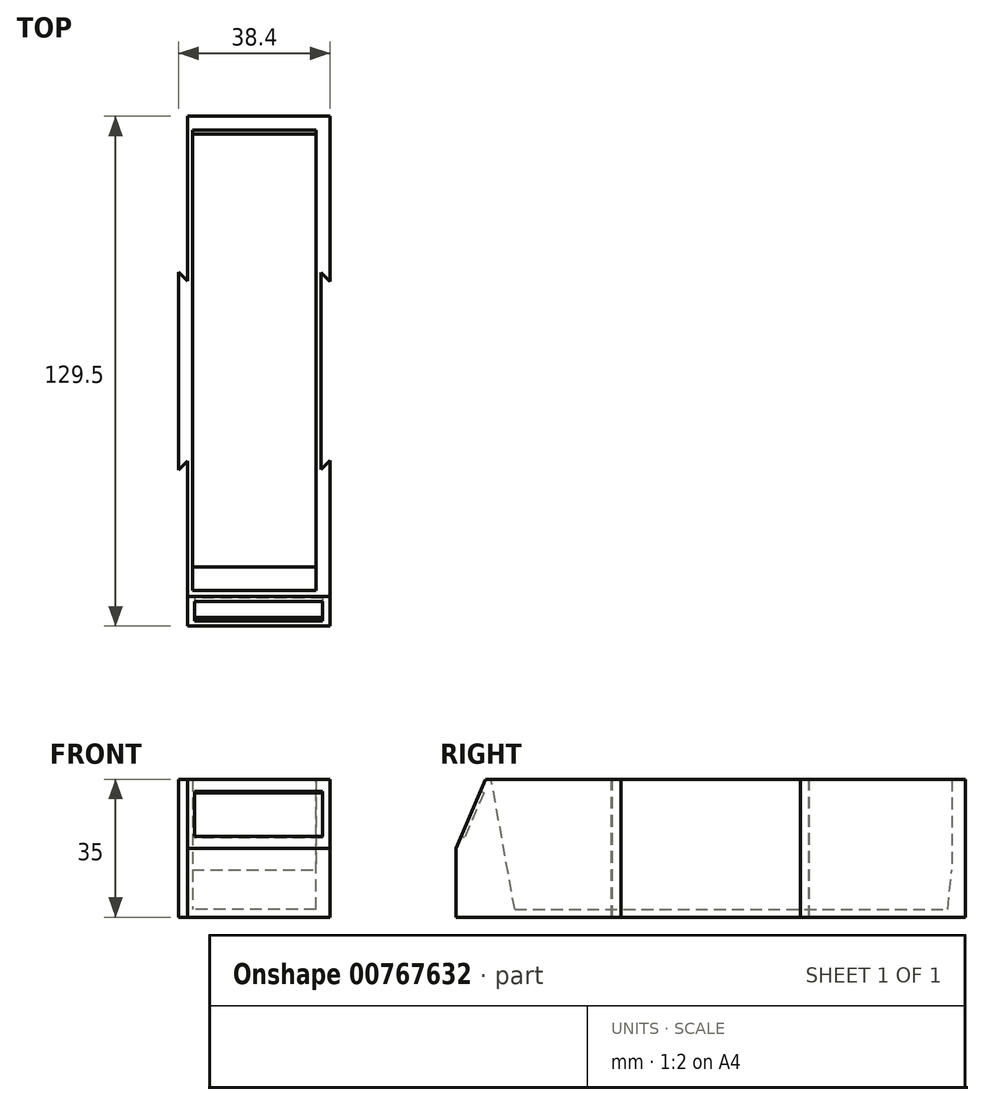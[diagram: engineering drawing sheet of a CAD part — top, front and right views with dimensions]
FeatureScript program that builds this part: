
annotation { "Feature Type Name" : "Feature", "Feature Type Description" : "" }
export const myFeature = defineFeature(function(context is Context, id is Id, definition is map)
    precondition{}
    {
        {
            var Q0;
            Q0=qCreatedBy(makeId("Top.planeOp"),FACE);
            var sketch = newSketch(context, id + "F0", { "sketchPlane" : qUnion([Q0])});
            skLineSegment(sketch, "E0.bottom", {"start": v(15.7, 55.5) * mm, "end": v(-15.7, 55.5) * mm});
            skLineSegment(sketch, "E0.top", {"start": v(15.7, -55.5) * mm, "end": v(-15.7, -55.5) * mm});
            skLineSegment(sketch, "E0.left", {"start": v(15.7, 55.5) * mm, "end": v(15.7, -55.5) * mm});
            skLineSegment(sketch, "E0.right", {"start": v(-15.7, 55.5) * mm, "end": v(-15.7, -55.5) * mm});
            skPoint(sketch, "E0.middle", {"position": v(0, 0) * mm});
            skLineSegment(sketch, "E1.bottom", {"start": v(19.2, -70.5) * mm, "end": v(-19.2, -70.5) * mm});
            skLineSegment(sketch, "E1.top", {"start": v(19.2, 59) * mm, "end": v(-19.2, 59) * mm});
            skLineSegment(sketch, "E1.left", {"start": v(19.2, -70.5) * mm, "end": v(19.2, 59) * mm});
            skLineSegment(sketch, "E1.right", {"start": v(-19.2, -70.5) * mm, "end": v(-19.2, 59) * mm});
            skPoint(sketch, "E1.middle", {"position": v(0, -5.75) * mm});
            skSolve(sketch);
        }
        {
            var Q0;
            Q0=qSketchRegion(id+"F0",true);
            var Q1;
            Q1=makeQuery(id+"F0.imprint","IMPRINT",FACE,{"disambiguationData":[TD([[makeQuery(id+"F0.imprint","IMPRINT",EDGE,{"derivedFrom":sQuery(id+"F0.wireOp",EDGE,"E0.bottom")}),1.0]])]});
            extrude(context, id + "F1", {"entities" : qUnion([Q0, Q1]), "depth" : 2 * mm, "offsetDistance" : 25 * mm});
        }
        {
            var Q0;
            Q0=makeQuery(id+"F0.imprint","IMPRINT",FACE,{"disambiguationData":[TD([[makeQuery(id+"F0.imprint","IMPRINT",EDGE,{"derivedFrom":sQuery(id+"F0.wireOp",EDGE,"E0.bottom")}),-1.0]])]});
            extrude(context, id + "F2", {"entities" : qUnion([Q0]), "operationType" : NewBodyOperationType.ADD, "depth" : 35 * mm, "offsetDistance" : 25 * mm});
        }
        {
            var Q0;
            Q0=makeQuery(id+"F2.opExtrude","CAP_EDGE",EDGE,{"disambiguationData":[OSD([sQuery(id+"F0.wireOp",EDGE,"E1.bottom")])],"isStart":false});
            chamfer(context, id + "F3", {"entities" : qUnion([Q0]), "chamferType" : ChamferType.TWO_OFFSETS, "width1" : 7.5 * mm, "oppositeDirection" : true, "width2" : 17.5 * mm, "tangentPropagation" : true});
        }
        {
            var Q0;
            Q0=makeQuery(id+"F2.opExtrude","CAP_EDGE",EDGE,{"disambiguationData":[OSD([sQuery(id+"F0.wireOp",EDGE,"E0.top")])],"isStart":false});
            chamfer(context, id + "F4", {"entities" : qUnion([Q0]), "chamferType" : ChamferType.TWO_OFFSETS, "width1" : 6 * mm, "oppositeDirection" : false, "width2" : 33 * mm, "tangentPropagation" : true});
        }
        {
            var Q0;
            Q0=makeQuery(id+"F2.opExtrude","CAP_FACE",FACE,{"disambiguationData":[OSD([sQuery(id+"F0.wireOp",EDGE,"E0.bottom"),sQuery(id+"F0.wireOp",EDGE,"E0.top"),sQuery(id+"F0.wireOp",EDGE,"E0.left"),sQuery(id+"F0.wireOp",EDGE,"E0.right"),sQuery(id+"F0.wireOp",EDGE,"E1.bottom"),sQuery(id+"F0.wireOp",EDGE,"E1.top"),sQuery(id+"F0.wireOp",EDGE,"E1.left"),sQuery(id+"F0.wireOp",EDGE,"E1.right")])],"isStart":false});
            var sketch = newSketch(context, id + "F5", { "sketchPlane" : qUnion([Q0])});
            skLineSegment(sketch, "E2", {"start": v(19.2, 17) * mm, "end": v(16.95, 19.25) * mm});
            skLineSegment(sketch, "E3", {"start": v(16.95, 19.25) * mm, "end": v(16.95, -30.75) * mm});
            skLineSegment(sketch, "E4", {"start": v(16.95, -30.75) * mm, "end": v(19.2, -28.5) * mm});
            skPoint(sketch, "E5", {"position": v(16.95, -5.75) * mm});
            skLineSegment(sketch, "E6", {"start": v(19.2, 17) * mm, "end": v(19.2, -28.5) * mm});
            skLineSegment(sketch, "E7", {"start": v(-19.2, 19.25) * mm, "end": v(-16.95, 17) * mm, "construction": true});
            skLineSegment(sketch, "E8", {"start": v(-19.2, -30.75) * mm, "end": v(-16.95, -28.5) * mm, "construction": true});
            skLineSegment(sketch, "E9", {"start": v(-16.95, -28.5) * mm, "end": v(-16.95, 17) * mm, "construction": true});
            skLineSegment(sketch, "E10", {"start": v(-16.95, 17) * mm, "end": v(-16.95, 59) * mm});
            skLineSegment(sketch, "E11", {"start": v(-16.95, 59) * mm, "end": v(-19.2, 59) * mm});
            skLineSegment(sketch, "E12", {"start": v(-19.2, 59) * mm, "end": v(-19.2, 19.25) * mm});
            skLineSegment(sketch, "E13", {"start": v(-16.95, -28.5) * mm, "end": v(-16.95, -70.5) * mm});
            skLineSegment(sketch, "E14", {"start": v(-16.95, -70.5) * mm, "end": v(-19.2, -70.5) * mm});
            skLineSegment(sketch, "E15", {"start": v(-19.2, -70.5) * mm, "end": v(-19.2, -30.75) * mm});
            skLineSegment(sketch, "E16", {"start": v(-19.2, 19.4) * mm, "end": v(-16.95, 17.14) * mm});
            skLineSegment(sketch, "E17", {"start": v(-19.2, -30.9) * mm, "end": v(-16.95, -28.64) * mm});
            skSolve(sketch);
        }
        {
            var Q0;
            Q0 = qSketchRegion(id + "F5", true);
            extrude(context, id + "F6", {"entities" : qUnion([Q0]), "operationType" : NewBodyOperationType.REMOVE, "endBound" : BoundingType.THROUGH_ALL, "oppositeDirection" : true, "depth" : 25 * mm, "offsetDistance" : 25 * mm});
        }
        {
            var Q0;
            Q0=makeQuery(id+"F3.opChamfer","BLEND_FACE",FACE,{"disambiguationData":[OSD([sQuery(id+"F0.wireOp",EDGE,"E1.bottom")])]});
            var sketch = newSketch(context, id + "F7", { "sketchPlane" : qUnion([Q0])});
            skLineSegment(sketch, "E18.bottom", {"start": v(17.37, 4.08) * mm, "end": v(-15.13, 4.08) * mm});
            skLineSegment(sketch, "E18.top", {"start": v(17.37, -8.42) * mm, "end": v(-15.13, -8.42) * mm});
            skLineSegment(sketch, "E18.left", {"start": v(17.37, 4.08) * mm, "end": v(17.37, -8.42) * mm});
            skLineSegment(sketch, "E18.right", {"start": v(-15.13, 4.08) * mm, "end": v(-15.13, -8.42) * mm});
            skPoint(sketch, "E18.middle", {"position": v(1.12, -2.17) * mm});
            skPoint(sketch, "E18.middle.positionSnap0", {"position": v(1.12, 7.35) * mm});
            skPoint(sketch, "E18.centerSnap0", {"position": v(1.12, 7.35) * mm});
            skSolve(sketch);
        }
        {
            var Q0;
            Q0 = qSketchRegion(id + "F7", true);
            extrude(context, id + "F8", {"entities" : qUnion([Q0]), "operationType" : NewBodyOperationType.REMOVE, "oppositeDirection" : true, "depth" : 1 * mm, "offsetDistance" : 25 * mm});
        }
        {
            var Q0;
            Q0=makeQuery(id+"F2.boolean.opBoolean","INTERSECT",EDGE,{"derivedFrom":[makeQuery(id+"F1.opExtrude","CAP_FACE",FACE,{"disambiguationData":[OSD([sQuery(id+"F0.wireOp",EDGE,"E1.bottom"),sQuery(id+"F0.wireOp",EDGE,"E1.top"),sQuery(id+"F0.wireOp",EDGE,"E1.left"),sQuery(id+"F0.wireOp",EDGE,"E1.right")])],"isStart":false}),makeQuery(id+"F2.opExtrude","SWEPT_FACE",FACE,{"disambiguationData":[OSD([sQuery(id+"F0.wireOp",EDGE,"E0.bottom")])]})]});
            chamfer(context, id + "F9", {"entities" : qUnion([Q0]), "chamferType" : ChamferType.TWO_OFFSETS, "width1" : 1 * mm, "oppositeDirection" : true, "width2" : 10 * mm, "tangentPropagation" : true});
        }
    });
